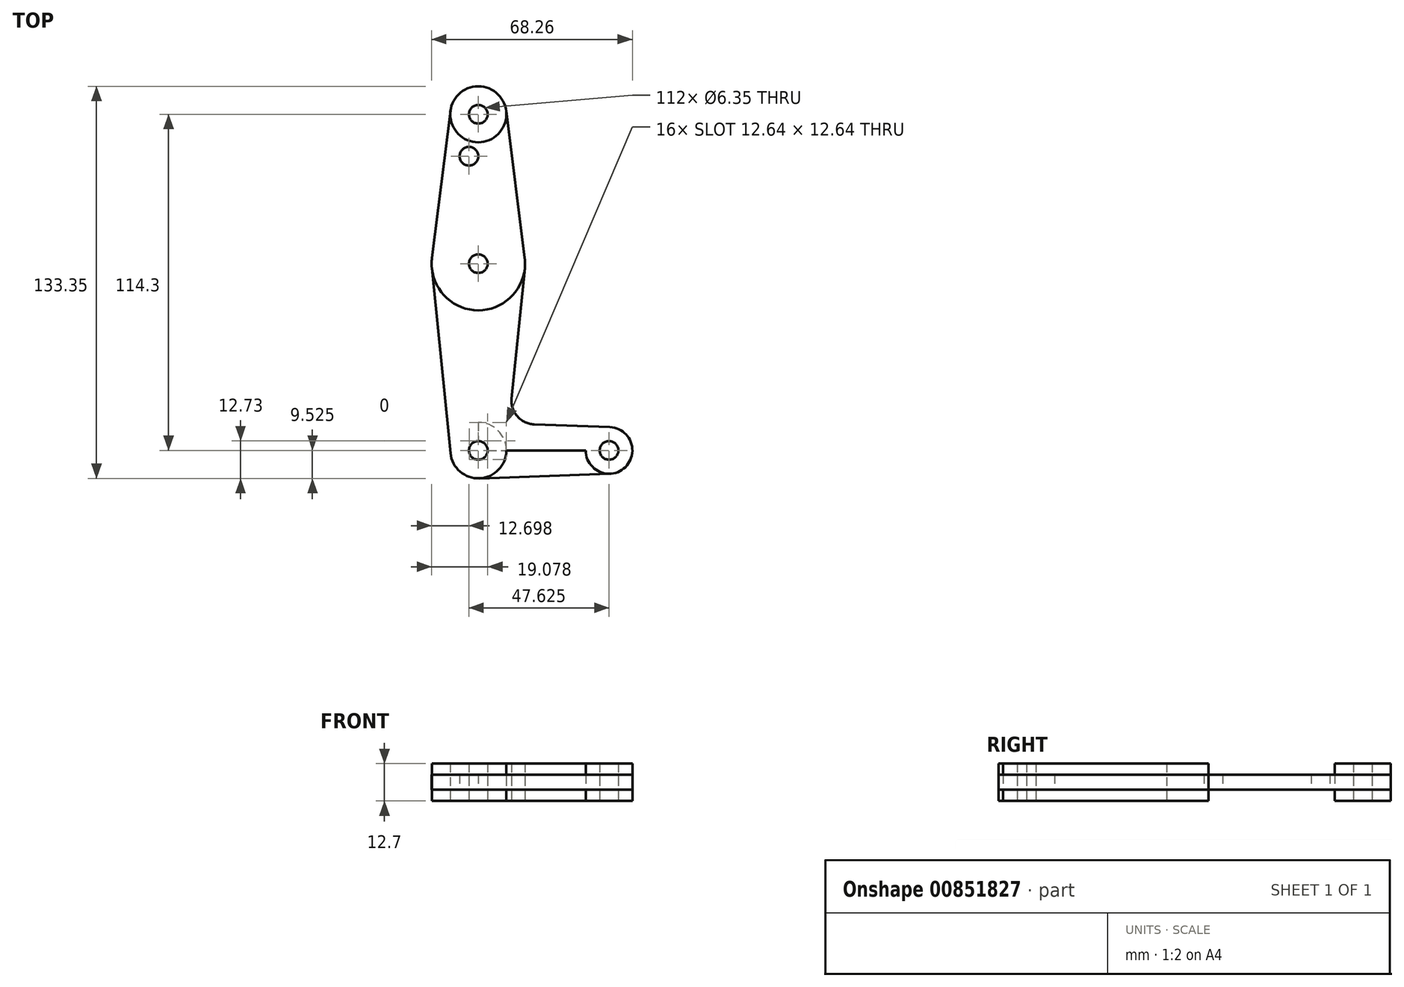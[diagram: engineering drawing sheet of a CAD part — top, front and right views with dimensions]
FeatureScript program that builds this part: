
annotation { "Feature Type Name" : "Feature", "Feature Type Description" : "" }
export const myFeature = defineFeature(function(context is Context, id is Id, definition is map)
    precondition{}
    {
        {
            var Q0;
            Q0=qCreatedBy(makeId("Top.planeOp"),FACE);
            var sketch = newSketch(context, id + "F0", { "sketchPlane" : qUnion([Q0])});
            skLineSegment(sketch, "E0", {"start": v(-9.48, 81.91) * mm, "end": v(-9.48, -32.39) * mm});
            skLineSegment(sketch, "E1", {"start": v(-9.48, -32.39) * mm, "end": v(34.97, -32.39) * mm});
            skCircle(sketch, "E2", {"center": v(34.97, -32.39) * mm, "radius": 7.94 * mm});
            skCircle(sketch, "E3", {"center": v(-9.48, -32.39) * mm, "radius": 9.53 * mm});
            skCircle(sketch, "E4", {"center": v(-9.48, 81.91) * mm, "radius": 9.53 * mm});
            skCircle(sketch, "E5", {"center": v(-9.48, 31.11) * mm, "radius": 15.88 * mm});
            skLineSegment(sketch, "E6", {"start": v(-0.03, 83.1) * mm, "end": v(6.27, 33.1) * mm});
            skLineSegment(sketch, "E7.MirrorCS", {"start": v(-18.93, 83.1) * mm, "end": v(-25.23, 33.1) * mm});
            skLineSegment(sketch, "E8", {"start": v(6.32, 29.53) * mm, "end": v(1.86, -14.8) * mm});
            skLineSegment(sketch, "E9.MirrorCS", {"start": v(-25.27, 29.53) * mm, "end": v(-18.95, -33.34) * mm});
            skLineSegment(sketch, "E10", {"start": v(-9.14, -41.9) * mm, "end": v(35.26, -40.32) * mm});
            skLineSegment(sketch, "E11.MirrorCS", {"start": v(9.5, -23.53) * mm, "end": v(35.26, -24.45) * mm});
            skCircle(sketch, "E12", {"center": v(-9.48, 81.91) * mm, "radius": 3.18 * mm});
            skCircle(sketch, "E13", {"center": v(-9.48, 31.11) * mm, "radius": 3.18 * mm});
            skCircle(sketch, "E14", {"center": v(-9.48, -32.39) * mm, "radius": 3.18 * mm});
            skCircle(sketch, "E15", {"center": v(34.97, -32.39) * mm, "radius": 3.18 * mm});
            skPoint(sketch, "E16.newPointA", {"position": v(0, -33.34) * mm});
            skPoint(sketch, "E16.newPointB", {"position": v(-9.14, -22.87) * mm});
            skArc(sketch, "E16.filletArc", {"start": v(1.86, -14.8) * mm, "mid": v(3.78, -20.81) * mm, "end": v(9.5, -23.53) * mm});
            skCircle(sketch, "E17", {"center": v(-12.65, 67.64) * mm, "radius": 3.18 * mm});
            skSolve(sketch);
        }
        {
            var Q0;
            Q0=makeQuery(id+"F0.imprint","IMPRINT",FACE,{"disambiguationData":[TD([[makeQuery(id+"F0.imprint","IMPRINT",EDGE,{"derivedFrom":sQuery(id+"F0.wireOp",EDGE,"E12")}),-1.0]])]});
            var Q1;
            {var subQ0=sQuery(id+"F0.wireOp",EDGE,"E5");var subQ4=sQuery(id+"F0.wireOp",EDGE,"E0");var subQ8=makeQuery(id+"F0.imprint","INTERSECT",VERTEX,{"disambiguationData":[OD(0.0)],"derivedFrom":[subQ4,subQ0]});Q1=makeQuery(id+"F0.imprint","IMPRINT",FACE,{"disambiguationData":[TD([[makeQuery(id+"F0.imprint","IMPRINT",EDGE,{"disambiguationData":[TD([[subQ8,-1.0]])],"derivedFrom":subQ4}),-1.0]])]});}
            var Q2;
            {var subQ0=sQuery(id+"F0.wireOp",EDGE,"E5");var subQ2=sQuery(id+"F0.wireOp",EDGE,"E0");var subQ5=makeQuery(id+"F0.imprint","INTERSECT",VERTEX,{"disambiguationData":[OD(0.0)],"derivedFrom":[subQ2,subQ0]});Q2=makeQuery(id+"F0.imprint","IMPRINT",FACE,{"disambiguationData":[TD([[makeQuery(id+"F0.imprint","IMPRINT",EDGE,{"disambiguationData":[TD([[subQ5,-1.0]])],"derivedFrom":subQ2}),1.0]])]});}
            var Q3;
            {var subQ0=sQuery(id+"F0.wireOp",EDGE,"E3");var subQ2=sQuery(id+"F0.wireOp",EDGE,"E0");var subQ3=makeQuery(id+"F0.imprint","INTERSECT",VERTEX,{"derivedFrom":[subQ2,subQ0]});Q3=makeQuery(id+"F0.imprint","IMPRINT",FACE,{"disambiguationData":[TD([[makeQuery(id+"F0.imprint","IMPRINT",EDGE,{"disambiguationData":[TD([[subQ3,-1.0]])],"derivedFrom":subQ2}),-1.0]])]});}
            var Q4;
            {var subQ0=sQuery(id+"F0.wireOp",EDGE,"E3");var subQ1=sQuery(id+"F0.wireOp",EDGE,"E0");var subQ2=makeQuery(id+"F0.imprint","INTERSECT",VERTEX,{"derivedFrom":[subQ1,subQ0]});Q4=makeQuery(id+"F0.imprint","IMPRINT",FACE,{"disambiguationData":[TD([[makeQuery(id+"F0.imprint","IMPRINT",EDGE,{"disambiguationData":[TD([[subQ2,-1.0]])],"derivedFrom":subQ1}),1.0]])]});}
            var Q5;
            Q5=makeQuery(id+"F0.imprint","IMPRINT",FACE,{"disambiguationData":[TD([[makeQuery(id+"F0.imprint","IMPRINT",EDGE,{"derivedFrom":sQuery(id+"F0.wireOp",EDGE,"E15")}),-1.0]])]});
            var Q6;
            Q6=sQuery(id+"F0.wireOp",EDGE,"E4");
            extrude(context, id + "F1", {"entities" : qUnion([Q0, Q1, Q2, Q3, Q4, Q5]), "surfaceEntities" : qUnion([Q6]), "endBound" : BoundingType.SYMMETRIC, "depth" : 12.7 * mm, "offsetDistance" : 25.4 * mm});
        }
        {
            var Q0;
            Q0 = qSketchRegion(id + "F0", true);
            extrude(context, id + "F2", {"entities" : qUnion([Q0]), "endBound" : BoundingType.SYMMETRIC, "depth" : 5.08 * mm, "offsetDistance" : 25.4 * mm});
        }
    });
